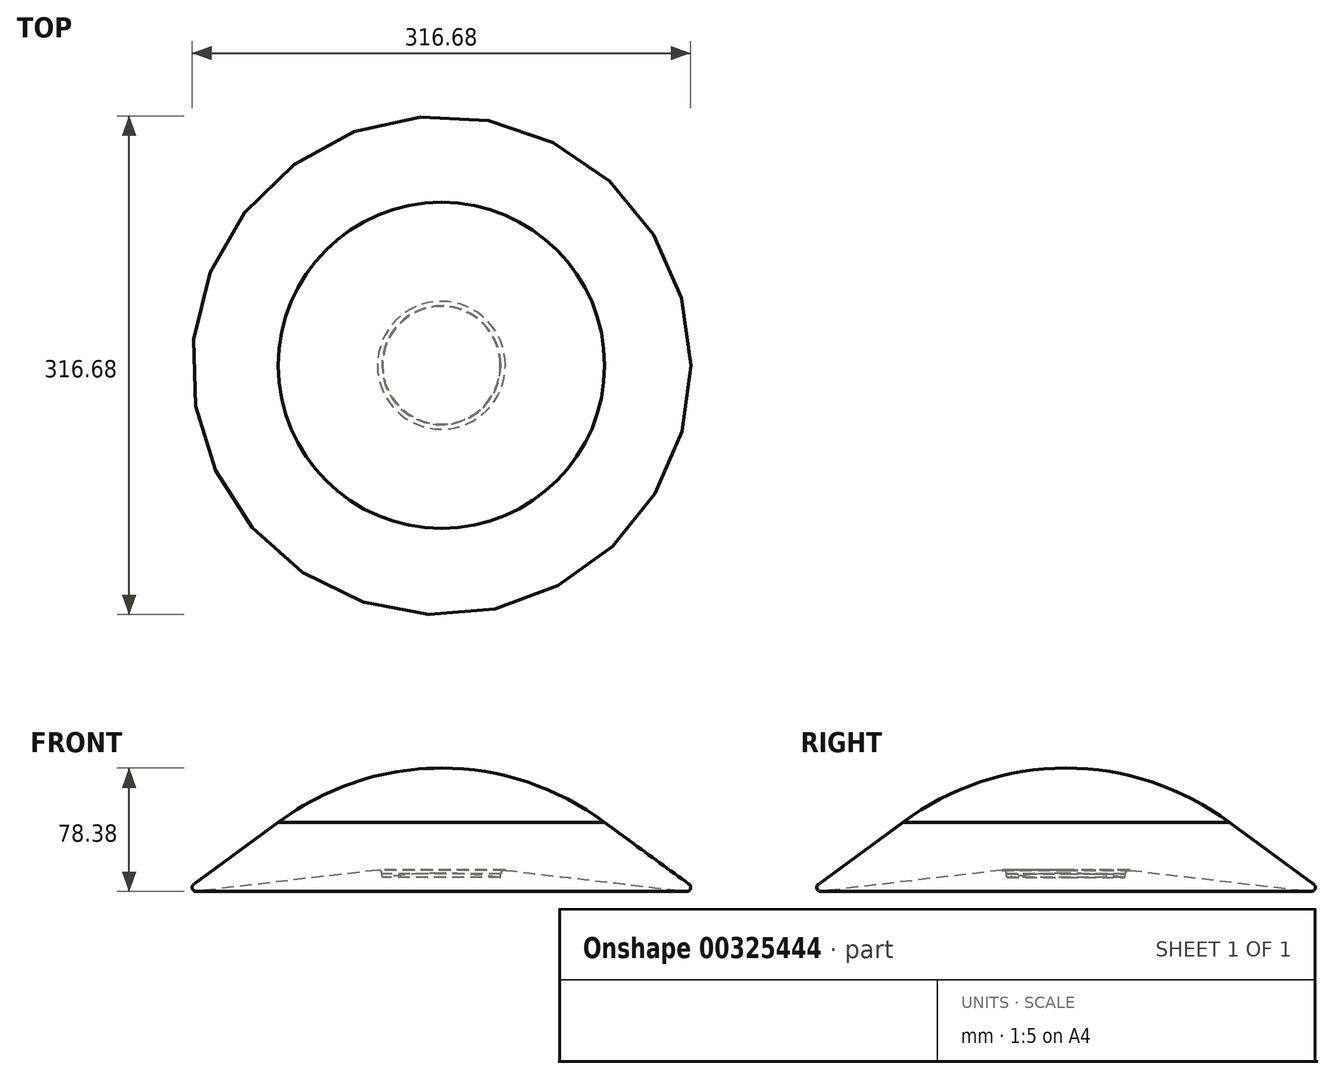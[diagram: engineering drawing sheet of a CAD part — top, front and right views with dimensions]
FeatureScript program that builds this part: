
annotation { "Feature Type Name" : "Feature", "Feature Type Description" : "" }
export const myFeature = defineFeature(function(context is Context, id is Id, definition is map)
    precondition{}
    {
        {
            var Q0;
            Q0=qCreatedBy(makeId("Front.planeOp"),FACE);
            var sketch = newSketch(context, id + "F0", { "sketchPlane" : qUnion([Q0])});
            skArc(sketch, "E0", {"start": v(24.46, 4.65) * mm, "mid": v(-24.55, 30.33) * mm, "end": v(-79.17, 39.2) * mm});
            skLineSegment(sketch, "E1", {"start": v(24.46, 4.65) * mm, "end": v(78.13, -34.6) * mm});
            skArc(sketch, "E2", {"start": v(-41.82, -30.37) * mm, "mid": v(-60.45, -28.3) * mm, "end": v(-79.17, -27.6) * mm});
            skLineSegment(sketch, "E3", {"start": v(76.33, -39.18) * mm, "end": v(-38.55, -25.64) * mm});
            skLineSegment(sketch, "E4", {"start": v(-41.45, -27.86) * mm, "end": v(-41.82, -30.37) * mm});
            skArc(sketch, "E5", {"start": v(-38.55, -25.64) * mm, "mid": v(-40.47, -26.14) * mm, "end": v(-41.45, -27.86) * mm});
            skArc(sketch, "E6", {"start": v(76.33, -39.18) * mm, "mid": v(79, -37.58) * mm, "end": v(78.13, -34.6) * mm});
            skLineSegment(sketch, "E7", {"start": v(-79.17, -27.6) * mm, "end": v(-79.17, 13.67) * mm});
            skSolve(sketch);
        }
        {
            var Q0;
            Q0=sQuery(id+"F0.wireOp",EDGE,"E3");
            var Q1;
            Q1=sQuery(id+"F0.wireOp",EDGE,"E1");
            var Q2;
            Q2=sQuery(id+"F0.wireOp",EDGE,"E6");
            var Q3;
            Q3=sQuery(id+"F0.wireOp",EDGE,"E4");
            var Q4;
            Q4=sQuery(id+"F0.wireOp",EDGE,"E5");
            var Q5;
            Q5=sQuery(id+"F0.wireOp",EDGE,"E0");
            var Q6;
            Q6=sQuery(id+"F0.wireOp",EDGE,"E2");
            var Q7;
            Q7=sQuery(id+"F0.wireOp",EDGE,"E7");
            revolve(context, id + "F1", {"bodyType" : ToolBodyType.SURFACE, "surfaceEntities" : qUnion([Q0, Q1, Q2, Q3, Q4, Q5, Q6]), "axis" : qUnion([Q7]), "revolveType" : RevolveType.FULL});
        }
    });
